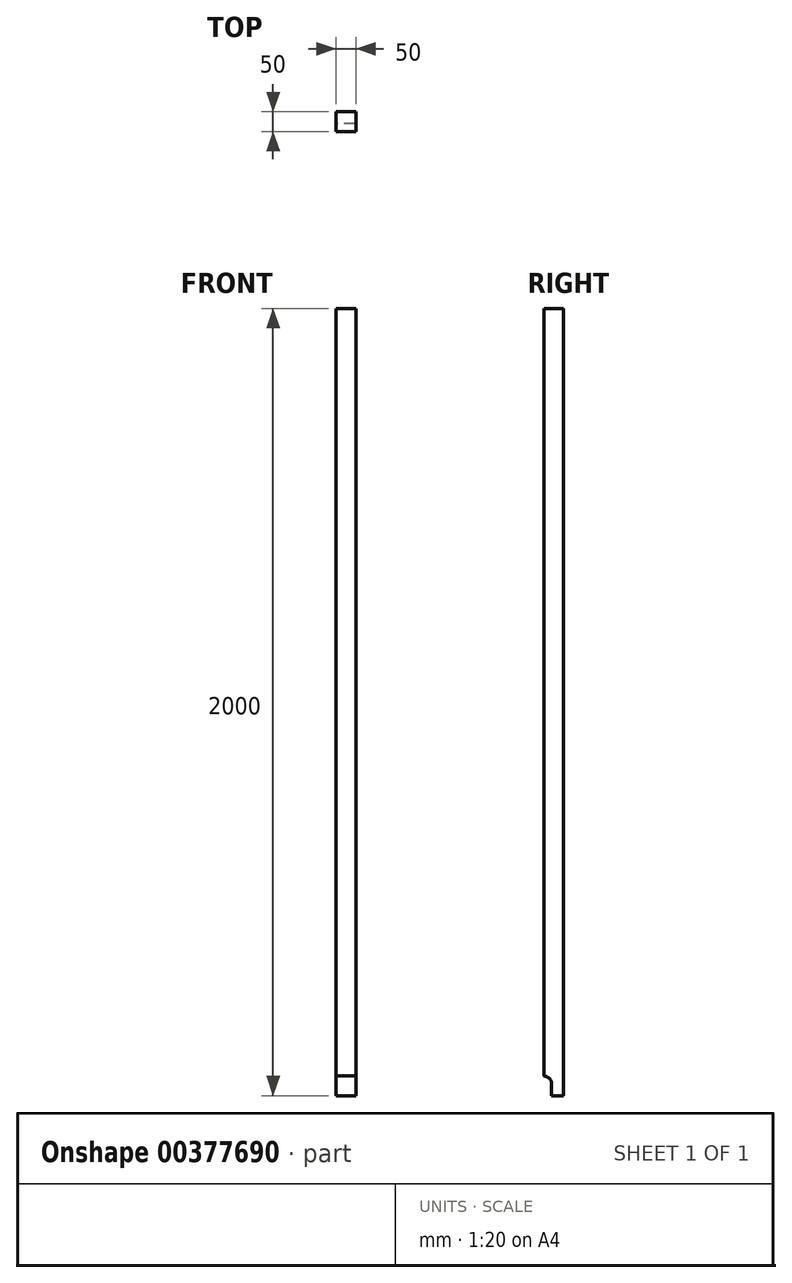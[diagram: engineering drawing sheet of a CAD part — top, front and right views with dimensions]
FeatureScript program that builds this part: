
annotation { "Feature Type Name" : "Feature", "Feature Type Description" : "" }
export const myFeature = defineFeature(function(context is Context, id is Id, definition is map)
    precondition{}
    {
        {
            var Q0;
            Q0=qCreatedBy(makeId("Top.planeOp"),FACE);
            var sketch = newSketch(context, id + "F0", { "sketchPlane" : qUnion([Q0])});
            skLineSegment(sketch, "E0.bottom", {"start": v(0, 0) * mm, "end": v(50, 0) * mm});
            skLineSegment(sketch, "E0.top", {"start": v(0, 50) * mm, "end": v(50, 50) * mm});
            skLineSegment(sketch, "E0.left", {"start": v(0, 0) * mm, "end": v(0, 50) * mm});
            skLineSegment(sketch, "E0.right", {"start": v(50, 0) * mm, "end": v(50, 50) * mm});
            skSolve(sketch);
        }
        {
            var Q0;
            Q0=makeQuery(id+"F0.imprint","IMPRINT",FACE,{"disambiguationData":[TD([[makeQuery(id+"F0.imprint","IMPRINT",EDGE,{"derivedFrom":sQuery(id+"F0.wireOp",EDGE,"E0.bottom")}),1.0]])]});
            extrude(context, id + "F1", {"entities" : qUnion([Q0]), "depth" : 2000 * mm});
        }
        {
            var Q0;
            Q0=qCreatedBy(makeId("Right.planeOp"),FACE);
            var sketch = newSketch(context, id + "F2", { "sketchPlane" : qUnion([Q0])});
            skLineSegment(sketch, "E1.bottom", {"start": v(0, 0) * mm, "end": v(20, 0) * mm});
            skLineSegment(sketch, "E1.top", {"start": v(0, 50) * mm, "end": v(0, 50) * mm});
            skLineSegment(sketch, "E1.left", {"start": v(0, 0) * mm, "end": v(0, 50) * mm});
            skLineSegment(sketch, "E1.right", {"start": v(20, 0) * mm, "end": v(20, 30) * mm});
            skPoint(sketch, "E2.visualSharp", {"position": v(20, 50) * mm});
            skArc(sketch, "E2.filletArc", {"start": v(20, 30) * mm, "mid": v(14.14, 44.14) * mm, "end": v(0, 50) * mm});
            skSolve(sketch);
        }
        {
            var Q0;
            Q0=makeQuery(id+"F2.imprint","IMPRINT",FACE,{"disambiguationData":[TD([[makeQuery(id+"F2.imprint","IMPRINT",EDGE,{"derivedFrom":sQuery(id+"F2.wireOp",EDGE,"E1.bottom")}),1.0]])]});
            extrude(context, id + "F3", {"entities" : qUnion([Q0]), "operationType" : NewBodyOperationType.REMOVE, "endBound" : BoundingType.THROUGH_ALL, "depth" : 25 * mm});
        }
    });
